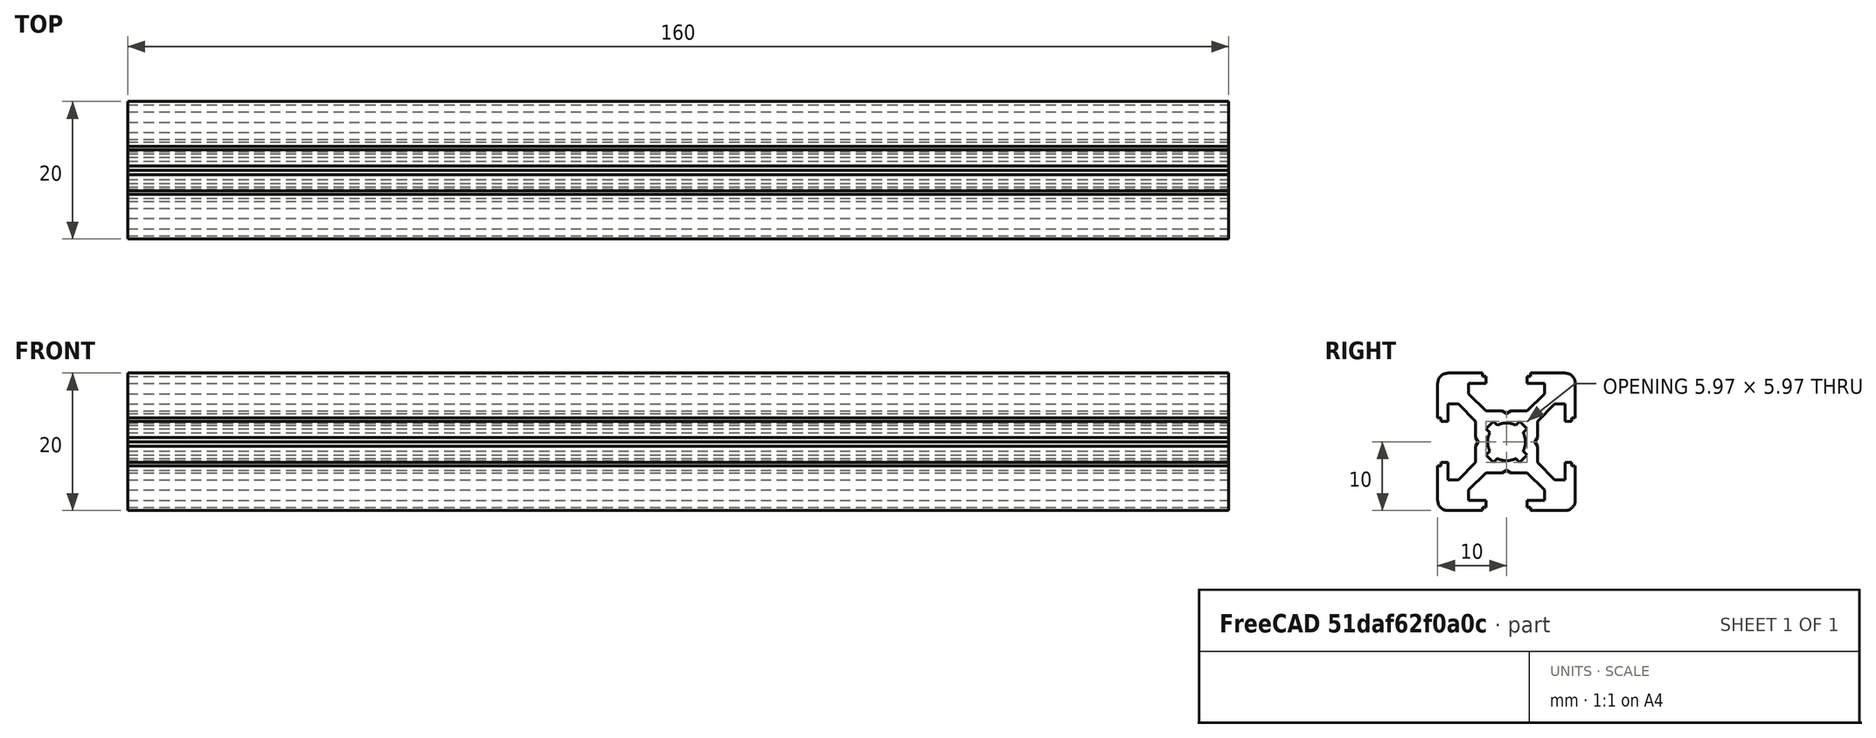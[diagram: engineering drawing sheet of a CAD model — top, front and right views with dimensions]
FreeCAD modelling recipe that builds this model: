
FCSTD DOCUMENT  (FreeCAD 0.19R)
Label: Tslot16
License: All rights reserved
LicenseURL: http://en.wikipedia.org/wiki/All_rights_reserved
objects: Sketcher::SketchObject×1, PartDesign::Pad×1, PartDesign::Body×1
note: 4 computed .brp shape members not serialized (recipe doc carries the construction recipe); baked Part::Feature solids carry a one-line shape summary decoded from their .brp

FEATURE [Sketcher::SketchObject] Sketch  label="T-Slot-Skizze"
  FullyConstrained = true
  MapMode = 5
  Placement = pos=(0,0,0) rot=(0.57735,0.57735,0.57735;2.0944rad)
  Support = -> [YZ_Plane]
  sketch-geometry (98):
    g0: LineSegment StartX=0 StartY=4.1 StartZ=0 EndX=0.65 EndY=4.5 EndZ=0
    g1: LineSegment StartX=0.65 StartY=4.5 StartZ=0 EndX=3 EndY=4.5 EndZ=0
    g2: LineSegment StartX=3 StartY=4.5 StartZ=0 EndX=5.5 EndY=7 EndZ=0
    g3: LineSegment StartX=5.5 StartY=7 StartZ=0 EndX=5.5 EndY=8.5 EndZ=0
    g4: LineSegment StartX=5.5 StartY=8.5 StartZ=0 EndX=3 EndY=8.5 EndZ=0
    g5: LineSegment StartX=3 StartY=8.5 StartZ=0 EndX=3 EndY=9.5 EndZ=0
    g6: LineSegment StartX=3 StartY=9.5 StartZ=0 EndX=3.5 EndY=9.5 EndZ=0
    g7: LineSegment StartX=3.5 StartY=9.5 StartZ=0 EndX=3.5 EndY=10 EndZ=0
    g8: LineSegment StartX=3.5 StartY=10 StartZ=0 EndX=8.5 EndY=10 EndZ=0
    g9: LineSegment StartX=10 StartY=8.5 StartZ=0 EndX=10 EndY=3.5 EndZ=0
    g10: LineSegment StartX=10 StartY=3.5 StartZ=0 EndX=9.5 EndY=3.5 EndZ=0
    g11: LineSegment StartX=9.5 StartY=3.5 StartZ=0 EndX=9.5 EndY=3 EndZ=0
    g12: LineSegment StartX=9.5 StartY=3 StartZ=0 EndX=8.5 EndY=3 EndZ=0
    g13: LineSegment StartX=8.5 StartY=3 StartZ=0 EndX=8.5 EndY=5.5 EndZ=0
    g14: LineSegment StartX=8.5 StartY=5.5 StartZ=0 EndX=7 EndY=5.5 EndZ=0
    g15: LineSegment StartX=7 StartY=5.5 StartZ=0 EndX=4.5 EndY=3 EndZ=0
    g16: LineSegment StartX=4.5 StartY=3 StartZ=0 EndX=4.5 EndY=0.65 EndZ=0
    g17: LineSegment StartX=4.5 StartY=0.65 StartZ=0 EndX=4.1 EndY=0 EndZ=0
    g18: ArcOfCircle CenterX=8.5 CenterY=8.5 CenterZ=0 NormalX=0 NormalY=0 NormalZ=1 AngleXU=0 Radius=1.5 StartAngle=0 EndAngle=1.5708
    g19: LineSegment StartX=0 StartY=-4.1 StartZ=0 EndX=0.65 EndY=-4.5 EndZ=0
    g20: LineSegment StartX=0.65 StartY=-4.5 StartZ=0 EndX=3 EndY=-4.5 EndZ=0
    g21: LineSegment StartX=3 StartY=-4.5 StartZ=0 EndX=5.5 EndY=-7 EndZ=0
    g22: LineSegment StartX=5.5 StartY=-7 StartZ=0 EndX=5.5 EndY=-8.5 EndZ=0
    g23: LineSegment StartX=5.5 StartY=-8.5 StartZ=0 EndX=3 EndY=-8.5 EndZ=0
    g24: LineSegment StartX=3 StartY=-8.5 StartZ=0 EndX=3 EndY=-9.5 EndZ=0
    g25: LineSegment StartX=3 StartY=-9.5 StartZ=0 EndX=3.5 EndY=-9.5 EndZ=0
    g26: LineSegment StartX=3.5 StartY=-9.5 StartZ=0 EndX=3.5 EndY=-10 EndZ=0
    g27: LineSegment StartX=3.5 StartY=-10 StartZ=0 EndX=8.5 EndY=-10 EndZ=0
    g28: LineSegment StartX=10 StartY=-8.5 StartZ=0 EndX=10 EndY=-3.5 EndZ=0
    g29: LineSegment StartX=10 StartY=-3.5 StartZ=0 EndX=9.5 EndY=-3.5 EndZ=0
    g30: LineSegment StartX=9.5 StartY=-3.5 StartZ=0 EndX=9.5 EndY=-3 EndZ=0
    g31: LineSegment StartX=9.5 StartY=-3 StartZ=0 EndX=8.5 EndY=-3 EndZ=0
    g32: LineSegment StartX=8.5 StartY=-3 StartZ=0 EndX=8.5 EndY=-5.5 EndZ=0
    g33: LineSegment StartX=8.5 StartY=-5.5 StartZ=0 EndX=7 EndY=-5.5 EndZ=0
    g34: LineSegment StartX=7 StartY=-5.5 StartZ=0 EndX=4.5 EndY=-3 EndZ=0
    g35: LineSegment StartX=4.5 StartY=-3 StartZ=0 EndX=4.5 EndY=-0.65 EndZ=0
    g36: ArcOfCircle CenterX=8.5 CenterY=-8.5 CenterZ=0 NormalX=0 NormalY=0 NormalZ=1 AngleXU=0 Radius=1.5 StartAngle=4.71239 EndAngle=6.28319
    g37: LineSegment StartX=4.5 StartY=-0.65 StartZ=0 EndX=4.1 EndY=0 EndZ=0
    g38: LineSegment StartX=0 StartY=-4.1 StartZ=0 EndX=-0.65 EndY=-4.5 EndZ=0
    g39: LineSegment StartX=-0.65 StartY=-4.5 StartZ=0 EndX=-3 EndY=-4.5 EndZ=0
    g40: LineSegment StartX=-3 StartY=-4.5 StartZ=0 EndX=-5.5 EndY=-7 EndZ=0
    g41: LineSegment StartX=-5.5 StartY=-7 StartZ=0 EndX=-5.5 EndY=-8.5 EndZ=0
    g42: LineSegment StartX=-5.5 StartY=-8.5 StartZ=0 EndX=-3 EndY=-8.5 EndZ=0
    g43: LineSegment StartX=-3 StartY=-8.5 StartZ=0 EndX=-3 EndY=-9.5 EndZ=0
    g44: LineSegment StartX=-3 StartY=-9.5 StartZ=0 EndX=-3.5 EndY=-9.5 EndZ=0
    g45: LineSegment StartX=-3.5 StartY=-9.5 StartZ=0 EndX=-3.5 EndY=-10 EndZ=0
    g46: LineSegment StartX=-3.5 StartY=-10 StartZ=0 EndX=-8.5 EndY=-10 EndZ=0
    g47: LineSegment StartX=-10 StartY=-8.5 StartZ=0 EndX=-10 EndY=-3.5 EndZ=0
    g48: LineSegment StartX=-10 StartY=-3.5 StartZ=0 EndX=-9.5 EndY=-3.5 EndZ=0
    g49: LineSegment StartX=-9.5 StartY=-3.5 StartZ=0 EndX=-9.5 EndY=-3 EndZ=0
    g50: LineSegment StartX=-9.5 StartY=-3 StartZ=0 EndX=-8.5 EndY=-3 EndZ=0
    g51: LineSegment StartX=-8.5 StartY=-3 StartZ=0 EndX=-8.5 EndY=-5.5 EndZ=0
    g52: LineSegment StartX=-8.5 StartY=-5.5 StartZ=0 EndX=-7 EndY=-5.5 EndZ=0
    g53: LineSegment StartX=-7 StartY=-5.5 StartZ=0 EndX=-4.5 EndY=-3 EndZ=0
    g54: LineSegment StartX=-4.5 StartY=-3 StartZ=0 EndX=-4.5 EndY=-0.65 EndZ=0
    g55: ArcOfCircle CenterX=-8.5 CenterY=-8.5 CenterZ=0 NormalX=0 NormalY=0 NormalZ=1 AngleXU=0 Radius=1.5 StartAngle=3.14159 EndAngle=4.71239
    g56: LineSegment StartX=-4.5 StartY=-0.65 StartZ=0 EndX=-4.1 EndY=0 EndZ=0
    g57: LineSegment StartX=-0.65 StartY=4.5 StartZ=0 EndX=-3 EndY=4.5 EndZ=0
    g58: LineSegment StartX=-3 StartY=4.5 StartZ=0 EndX=-5.5 EndY=7 EndZ=0
    g59: LineSegment StartX=-5.5 StartY=7 StartZ=0 EndX=-5.5 EndY=8.5 EndZ=0
    g60: LineSegment StartX=-5.5 StartY=8.5 StartZ=0 EndX=-3 EndY=8.5 EndZ=0
    g61: LineSegment StartX=-3 StartY=8.5 StartZ=0 EndX=-3 EndY=9.5 EndZ=0
    g62: LineSegment StartX=-3 StartY=9.5 StartZ=0 EndX=-3.5 EndY=9.5 EndZ=0
    g63: LineSegment StartX=-3.5 StartY=9.5 StartZ=0 EndX=-3.5 EndY=10 EndZ=0
    g64: LineSegment StartX=-3.5 StartY=10 StartZ=0 EndX=-8.5 EndY=10 EndZ=0
    g65: LineSegment StartX=-10 StartY=8.5 StartZ=0 EndX=-10 EndY=3.5 EndZ=0
    g66: LineSegment StartX=-10 StartY=3.5 StartZ=0 EndX=-9.5 EndY=3.5 EndZ=0
    g67: LineSegment StartX=-9.5 StartY=3.5 StartZ=0 EndX=-9.5 EndY=3 EndZ=0
    g68: LineSegment StartX=-9.5 StartY=3 StartZ=0 EndX=-8.5 EndY=3 EndZ=0
    g69: LineSegment StartX=-8.5 StartY=3 StartZ=0 EndX=-8.5 EndY=5.5 EndZ=0
    g70: LineSegment StartX=-8.5 StartY=5.5 StartZ=0 EndX=-7 EndY=5.5 EndZ=0
    g71: LineSegment StartX=-7 StartY=5.5 StartZ=0 EndX=-4.5 EndY=3 EndZ=0
    g72: LineSegment StartX=-4.5 StartY=3 StartZ=0 EndX=-4.5 EndY=0.65 EndZ=0
    g73: ArcOfCircle CenterX=-8.5 CenterY=8.5 CenterZ=0 NormalX=0 NormalY=0 NormalZ=1 AngleXU=0 Radius=1.5 StartAngle=1.5708 EndAngle=3.14159
    g74: LineSegment StartX=-4.5 StartY=0.65 StartZ=0 EndX=-4.1 EndY=0 EndZ=0
    g75: LineSegment StartX=0 StartY=4.1 StartZ=0 EndX=-0.65 EndY=4.5 EndZ=0
    g76: Circle CenterX=0 CenterY=0 CenterZ=0 NormalX=0 NormalY=0 NormalZ=1 AngleXU=0 Radius=3.55
    g77: Circle CenterX=0 CenterY=0 CenterZ=0 NormalX=0 NormalY=0 NormalZ=1 AngleXU=0 Radius=2.75
    g78: LineSegment StartX=1.3405 StartY=2.40116 StartZ=0 EndX=1.92324 EndY=2.9839 EndZ=0
    g79: LineSegment StartX=1.92324 StartY=2.9839 StartZ=0 EndX=2.9839 EndY=1.92324 EndZ=0
    g80: LineSegment StartX=2.9839 StartY=1.92324 StartZ=0 EndX=2.40116 EndY=1.3405 EndZ=0
    g81: ArcOfCircle CenterX=0 CenterY=0 CenterZ=0 NormalX=0 NormalY=0 NormalZ=1 AngleXU=0 Radius=2.75 StartAngle=0 EndAngle=0.509172
    g82: ArcOfCircle CenterX=0 CenterY=0 CenterZ=0 NormalX=0 NormalY=0 NormalZ=1 AngleXU=0 Radius=2.75 StartAngle=1.06162 EndAngle=1.5708
    g83: LineSegment StartX=-1.3405 StartY=2.40116 StartZ=0 EndX=-1.92324 EndY=2.9839 EndZ=0
    g84: LineSegment StartX=-1.92324 StartY=2.9839 StartZ=0 EndX=-2.9839 EndY=1.92324 EndZ=0
    g85: LineSegment StartX=-2.9839 StartY=1.92324 StartZ=0 EndX=-2.40116 EndY=1.3405 EndZ=0
    g86: ArcOfCircle CenterX=-1.3e-15 CenterY=6e-16 CenterZ=0 NormalX=0 NormalY=0 NormalZ=1 AngleXU=0 Radius=2.75 StartAngle=2.63242 EndAngle=3.14159
    g87: ArcOfCircle CenterX=-1.3e-15 CenterY=6e-16 CenterZ=0 NormalX=0 NormalY=0 NormalZ=1 AngleXU=0 Radius=2.75 StartAngle=1.5708 EndAngle=2.07997
    g88: LineSegment StartX=-1.34051 StartY=-2.40115 StartZ=0 EndX=-1.92325 EndY=-2.98389 EndZ=0
    g89: LineSegment StartX=-1.92325 StartY=-2.98389 StartZ=0 EndX=-2.9839 EndY=-1.92323 EndZ=0
    g90: LineSegment StartX=-2.9839 StartY=-1.92323 StartZ=0 EndX=-2.40116 EndY=-1.34049 EndZ=0
    g91: ArcOfCircle CenterX=-3e-16 CenterY=2e-16 CenterZ=0 NormalX=0 NormalY=0 NormalZ=1 AngleXU=0 Radius=2.75 StartAngle=3.14159 EndAngle=3.65076
    g92: ArcOfCircle CenterX=-3e-16 CenterY=2e-16 CenterZ=0 NormalX=0 NormalY=0 NormalZ=1 AngleXU=0 Radius=2.75 StartAngle=4.20321 EndAngle=4.71239
    g93: LineSegment StartX=1.34051 StartY=-2.40115 StartZ=0 EndX=1.92325 EndY=-2.98389 EndZ=0
    g94: LineSegment StartX=1.92325 StartY=-2.98389 StartZ=0 EndX=2.9839 EndY=-1.92323 EndZ=0
    g95: LineSegment StartX=2.9839 StartY=-1.92323 StartZ=0 EndX=2.40116 EndY=-1.34049 EndZ=0
    g96: ArcOfCircle CenterX=3e-16 CenterY=2e-16 CenterZ=0 NormalX=0 NormalY=0 NormalZ=1 AngleXU=0 Radius=2.75 StartAngle=4.71239 EndAngle=5.22156
    g97: ArcOfCircle CenterX=3e-16 CenterY=2e-16 CenterZ=0 NormalX=0 NormalY=0 NormalZ=1 AngleXU=0 Radius=2.75 StartAngle=5.77402 EndAngle=6.28319
  constraints (291):
    c: PointOnObject(g0,g-2)
    c: Coincident(g0,g1)
    c: Horizontal(g1)
    c: Coincident(g1,g2)
    c: Coincident(g2,g3)
    c: Vertical(g3)
    c: Coincident(g3,g4)
    c: Horizontal(g4)
    c: Coincident(g4,g5)
    c: Vertical(g5)
    c: Coincident(g5,g6)
    c: Horizontal(g6)
    c: Coincident(g6,g7)
    c: Coincident(g7,g8)
    c: Horizontal(g8)
    c: Vertical(g7)
    c: DistanceX(g-1,g5) = 3
    c: DistanceY(g4,g7) = 1.5
    c: DistanceY(g0,g7) = 5.5
    c: DistanceY(g3,g3) = 1.5
    c: DistanceY(g4,g5) = 1
    c: DistanceX(g-1,g1) = 3
    c: DistanceX(g-1,g7) = 3.5
    c: DistanceX(g0,g0) = 0.65
    c: DistanceY(g0,g0) = 0.4
    c: DistanceX(g-1,g3) = 5.5
    c: Vertical(g9)
    c: Coincident(g9,g10)
    c: Coincident(g10,g11)
    c: Coincident(g11,g12)
    c: Coincident(g12,g13)
    c: Vertical(g13)
    c: Coincident(g13,g14)
    c: Horizontal(g14)
    c: Coincident(g14,g15)
    c: Coincident(g15,g16)
    c: Vertical(g16)
    c: Coincident(g16,g17)
    c: PointOnObject(g17,g-1)
    c: Horizontal(g10)
    c: Horizontal(g12)
    c: Vertical(g11)
    c: Equal(g17,g0)
    c: Equal(g1,g16)
    c: Equal(g15,g2)
    c: Equal(g3,g14)
    c: Equal(g13,g4)
    c: Equal(g12,g5)
    c: Parallel(g15,g2)
    c: Equal(g11,g6)
    c: Equal(g10,g7)
    c: Equal(g9,g8)
    c: Tangent(g8,g18) = 1.5708
    c: Tangent(g9,g18) = 1.5708
    c: Radius(g18) = 1.5
    c: DistanceY(g-1,g8) = 10
    c: DistanceX(g-1,g9) = 10
    c: Coincident(g19,g20)
    c: Horizontal(g20)
    c: Coincident(g20,g21)
    c: Coincident(g21,g22)
    c: Vertical(g22)
    c: Coincident(g22,g23)
    c: Horizontal(g23)
    c: Coincident(g23,g24)
    c: Vertical(g24)
    c: Coincident(g24,g25)
    c: Horizontal(g25)
    c: Coincident(g25,g26)
    c: Coincident(g26,g27)
    c: Horizontal(g27)
    c: Vertical(g26)
    c: Vertical(g28)
    c: Coincident(g28,g29)
    c: Coincident(g29,g30)
    c: Coincident(g30,g31)
    c: Coincident(g31,g32)
    c: Vertical(g32)
    c: Coincident(g32,g33)
    c: Horizontal(g33)
    c: Coincident(g33,g34)
    c: Coincident(g34,g35)
    c: Vertical(g35)
    c: Coincident(g35,g37)
    c: Horizontal(g29)
    c: Horizontal(g31)
    c: Vertical(g30)
    c: Equal(g37,g19)
    c: Equal(g20,g35)
    c: Equal(g34,g21)
    c: Equal(g22,g33)
    c: Equal(g32,g23)
    c: Equal(g31,g24)
    c: Parallel(g34,g21)
    c: Equal(g30,g25)
    c: Equal(g29,g26)
    c: Equal(g28,g27)
    c: Tangent(g27,g36) = -1.5708
    c: Tangent(g28,g36) = -1.5708
    c: Radius(g36) = 1.5
    c: Equal(g9,g28)
    c: Equal(g12,g31)
    c: DistanceX(g-1,g28) = 10
    c: DistanceY(g27,g-1) = 10
    c: DistanceY(g30,g-1) = 3
    c: Equal(g33,g14)
    c: Equal(g35,g16)
    c: Equal(g17,g37)
    c: Coincident(g37,g17)
    c: Equal(g15,g34)
    c: PointOnObject(g19,g-2)
    c: DistanceY(g34,g-1) = 3
    c: DistanceX(g-1,g20) = 3
    c: Coincident(g38,g39)
    c: Horizontal(g39)
    c: Coincident(g39,g40)
    c: Coincident(g40,g41)
    c: Vertical(g41)
    c: Coincident(g41,g42)
    c: Horizontal(g42)
    c: Coincident(g42,g43)
    c: Vertical(g43)
    c: Coincident(g43,g44)
    c: Horizontal(g44)
    c: Coincident(g44,g45)
    c: Coincident(g45,g46)
    c: Horizontal(g46)
    c: Vertical(g45)
    c: Vertical(g47)
    c: Coincident(g47,g48)
    c: Coincident(g48,g49)
    c: Coincident(g49,g50)
    c: Coincident(g50,g51)
    c: Vertical(g51)
    c: Coincident(g51,g52)
    c: Horizontal(g52)
    c: Coincident(g52,g53)
    c: Coincident(g53,g54)
    c: Vertical(g54)
    c: Coincident(g54,g56)
    c: Horizontal(g48)
    c: Horizontal(g50)
    c: Vertical(g49)
    c: Equal(g39,g54)
    c: Equal(g53,g40)
    c: Equal(g41,g52)
    c: Equal(g51,g42)
    c: Equal(g50,g43)
    c: Parallel(g53,g40)
    c: Equal(g49,g44)
    c: Equal(g48,g45)
    c: Equal(g47,g46)
    c: Tangent(g46,g55) = 1.5708
    c: Tangent(g47,g55) = 1.5708
    c: Radius(g55) = 1.5
    c: Coincident(g38,g19)
    c: DistanceX(g39,g-1) = 3
    c: DistanceX(g38,g19) = 0.65
    c: DistanceY(g38,g19) = 0.4
    c: PointOnObject(g56,g-1)
    c: Equal(g56,g38)
    c: DistanceY(g53,g-1) = 3
    c: Equal(g22,g41)
    c: Equal(g42,g23)
    c: Equal(g24,g43)
    c: Equal(g25,g44)
    c: Equal(g26,g45)
    c: DistanceY(g46,g-1) = 10
    c: DistanceX(g47,g-1) = 10
    c: Coincident(g75,g57)
    c: Horizontal(g57)
    c: Coincident(g57,g58)
    c: Coincident(g58,g59)
    c: Vertical(g59)
    c: Coincident(g59,g60)
    c: Horizontal(g60)
    c: Coincident(g60,g61)
    c: Vertical(g61)
    c: Coincident(g61,g62)
    c: Horizontal(g62)
    c: Coincident(g62,g63)
    c: Coincident(g63,g64)
    c: Horizontal(g64)
    c: Vertical(g63)
    c: Vertical(g65)
    c: Coincident(g65,g66)
    c: Coincident(g66,g67)
    c: Coincident(g67,g68)
    c: Coincident(g68,g69)
    c: Vertical(g69)
    c: Coincident(g69,g70)
    c: Horizontal(g70)
    c: Coincident(g70,g71)
    c: Coincident(g71,g72)
    c: Vertical(g72)
    c: Coincident(g72,g74)
    c: Horizontal(g66)
    c: Horizontal(g68)
    c: Vertical(g67)
    c: Equal(g57,g72)
    c: Equal(g71,g58)
    c: Equal(g59,g70)
    c: Equal(g69,g60)
    c: Equal(g68,g61)
    c: Parallel(g71,g58)
    c: Equal(g67,g62)
    c: Equal(g66,g63)
    c: Equal(g65,g64)
    c: Tangent(g64,g73) = -1.5708
    c: Tangent(g65,g73) = -1.5708
    c: Radius(g73) = 1.5
    c: Equal(g74,g75)
    c: Coincident(g56,g74)
    c: Coincident(g0,g75)
    c: Equal(g0,g75)
    c: Equal(g1,g57)
    c: Equal(g2,g58)
    c: Equal(g3,g59)
    c: Equal(g4,g60)
    c: Equal(g5,g61)
    c: Equal(g6,g62)
    c: Equal(g7,g63)
    c: Equal(g8,g64)
    c: DistanceX(g65,g-1) = 10
    c: Coincident(g76,g-1)
    c: Coincident(g77,g-1)
    c: Radius(g76) = 3.55
    c: Radius(g77) = 2.75
    c: PointOnObject(g78,g77)
    c: PointOnObject(g78,g76)
    c: Coincident(g78,g79)
    c: PointOnObject(g79,g76)
    c: Coincident(g79,g80)
    c: PointOnObject(g80,g77)
    c: Coincident(g81,g-1)
    c: Coincident(g81,g80)
    c: Coincident(g82,g81)
    c: Coincident(g82,g78)
    c: Parallel(g78,g80)
    c: Parallel(g78,g2)
    c: Distance(g79) = 1.5
    c: Distance(g78,g80) = 1.5
    c: PointOnObject(g82,g-2)
    c: PointOnObject(g81,g-1)
    c: Coincident(g83,g84)
    c: Coincident(g84,g85)
    c: Coincident(g86,g85)
    c: Coincident(g87,g86)
    c: Coincident(g87,g83)
    c: Parallel(g83,g85)
    c: Distance(g84) = 1.5
    c: Distance(g83,g85) = 1.5
    c: Coincident(g82,g87)
    c: PointOnObject(g86,g-1)
    c: PointOnObject(g83,g76)
    c: PointOnObject(g83,g77)
    c: PointOnObject(g85,g77)
    c: PointOnObject(g84,g76)
    c: PointOnObject(g86,g77)
    c: Parallel(g85,g71)
    c: Coincident(g88,g89)
    c: Coincident(g89,g90)
    c: Coincident(g91,g90)
    c: Coincident(g92,g91)
    c: Coincident(g92,g88)
    c: Parallel(g88,g90)
    c: Distance(g89) = 1.5
    c: Distance(g88,g90) = 1.5
    c: PointOnObject(g88,g77)
    c: PointOnObject(g90,g77)
    c: Coincident(g86,g91)
    c: PointOnObject(g89,g76)
    c: PointOnObject(g88,g76)
    c: PointOnObject(g92,g-2)
    c: PointOnObject(g92,g77)
    c: Parallel(g88,g40)
    c: Coincident(g93,g94)
    c: Coincident(g94,g95)
    c: Coincident(g97,g95)
    c: Coincident(g96,g97)
    c: Coincident(g96,g93)
    c: Parallel(g93,g95)
    c: Distance(g94) = 1.5
    c: Distance(g93,g95) = 1.5
    c: Coincident(g81,g97)
    c: Coincident(g92,g96)
    c: PointOnObject(g93,g77)
    c: PointOnObject(g95,g77)
    c: PointOnObject(g94,g76)
    c: PointOnObject(g93,g76)
    c: Parallel(g93,g21)
FEATURE [PartDesign::Pad] Pad  label="T-Slot-Element"
  Direction = (1,1,1)
  Length = 160
  Length2 = 100
  Placement = pos=(0,0,0) rot=(0.57735,0.57735,0.57735;2.0944rad)
  Profile = -> Sketch
  Type = 0
FEATURE [PartDesign::Body] Body  label="T-Slot-Profil 20x20"
  Group = -> [Sketch,Pad]
  Origin = -> Origin
  Tip = -> Pad
